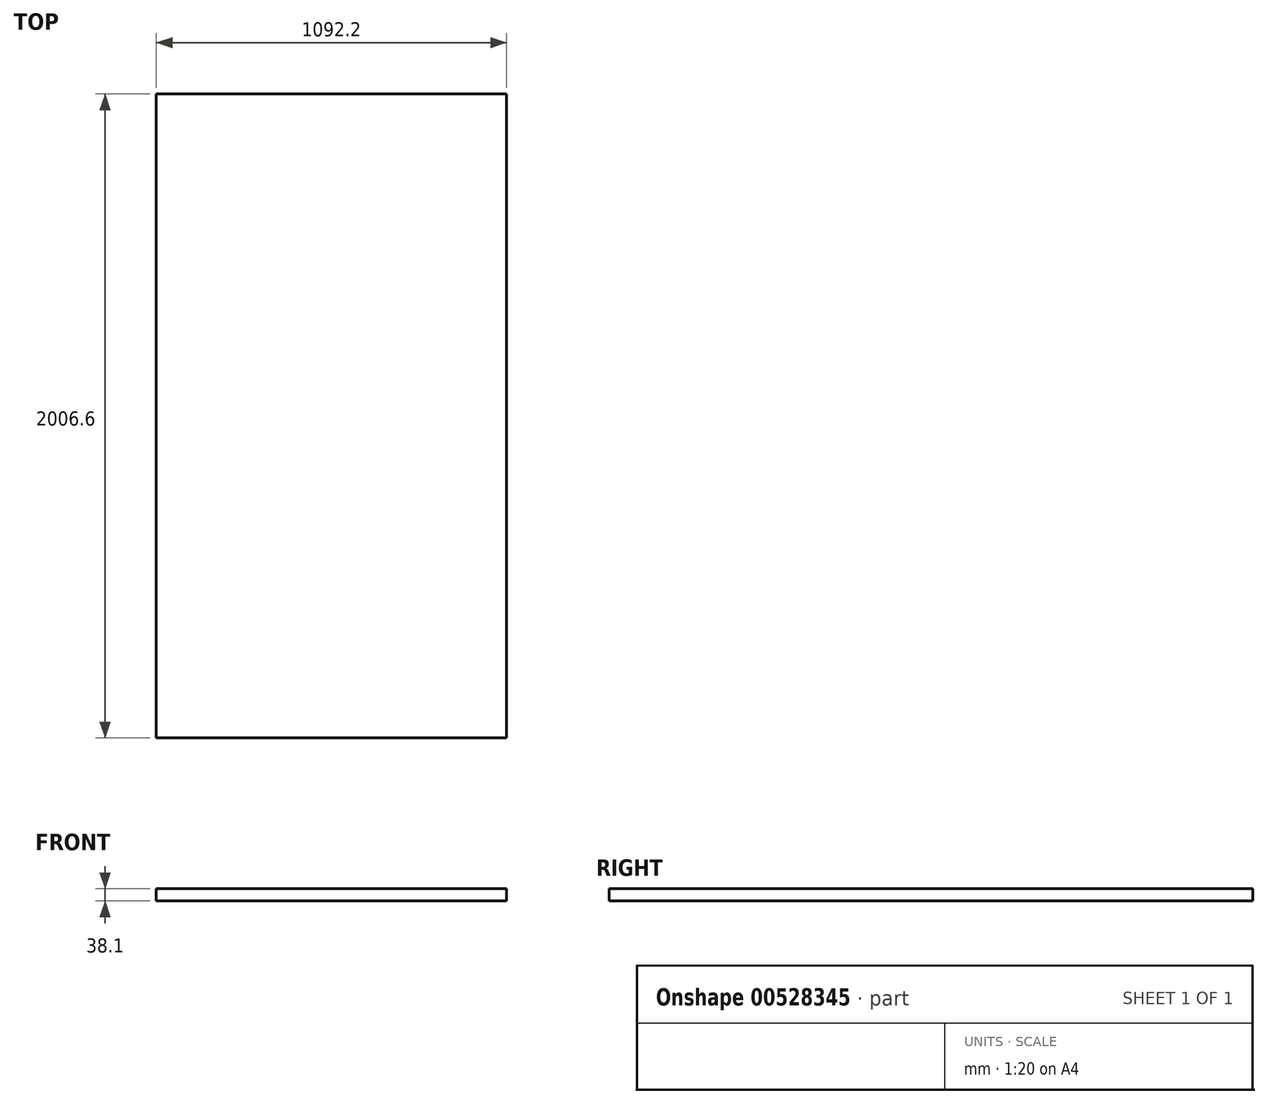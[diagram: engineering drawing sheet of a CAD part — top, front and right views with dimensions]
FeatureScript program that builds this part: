
annotation { "Feature Type Name" : "Feature", "Feature Type Description" : "" }
export const myFeature = defineFeature(function(context is Context, id is Id, definition is map)
    precondition{}
    {
        {
            var Q0;
            Q0=qCreatedBy(makeId("Top.planeOp"),FACE);
            var sketch = newSketch(context, id + "F0", { "sketchPlane" : qUnion([Q0])});
            skLineSegment(sketch, "E0.bottom", {"start": v(0, 0) * mm, "end": v(-1092.2, 0) * mm});
            skLineSegment(sketch, "E0.top", {"start": v(0, -2006.6) * mm, "end": v(-1092.2, -2006.6) * mm});
            skLineSegment(sketch, "E0.left", {"start": v(0, 0) * mm, "end": v(0, -2006.6) * mm});
            skLineSegment(sketch, "E0.right", {"start": v(-1092.2, 0) * mm, "end": v(-1092.2, -2006.6) * mm});
            skSolve(sketch);
        }
        {
            var Q0;
            Q0=makeQuery(id+"F0.imprint","IMPRINT",FACE,{"disambiguationData":[TD([[makeQuery(id+"F0.imprint","IMPRINT",EDGE,{"derivedFrom":sQuery(id+"F0.wireOp",EDGE,"E0.bottom")}),1.0]])]});
            extrude(context, id + "F1", {"entities" : qUnion([Q0]), "depth" : 38.1 * mm, "offsetDistance" : 25.4 * mm});
        }
    });
